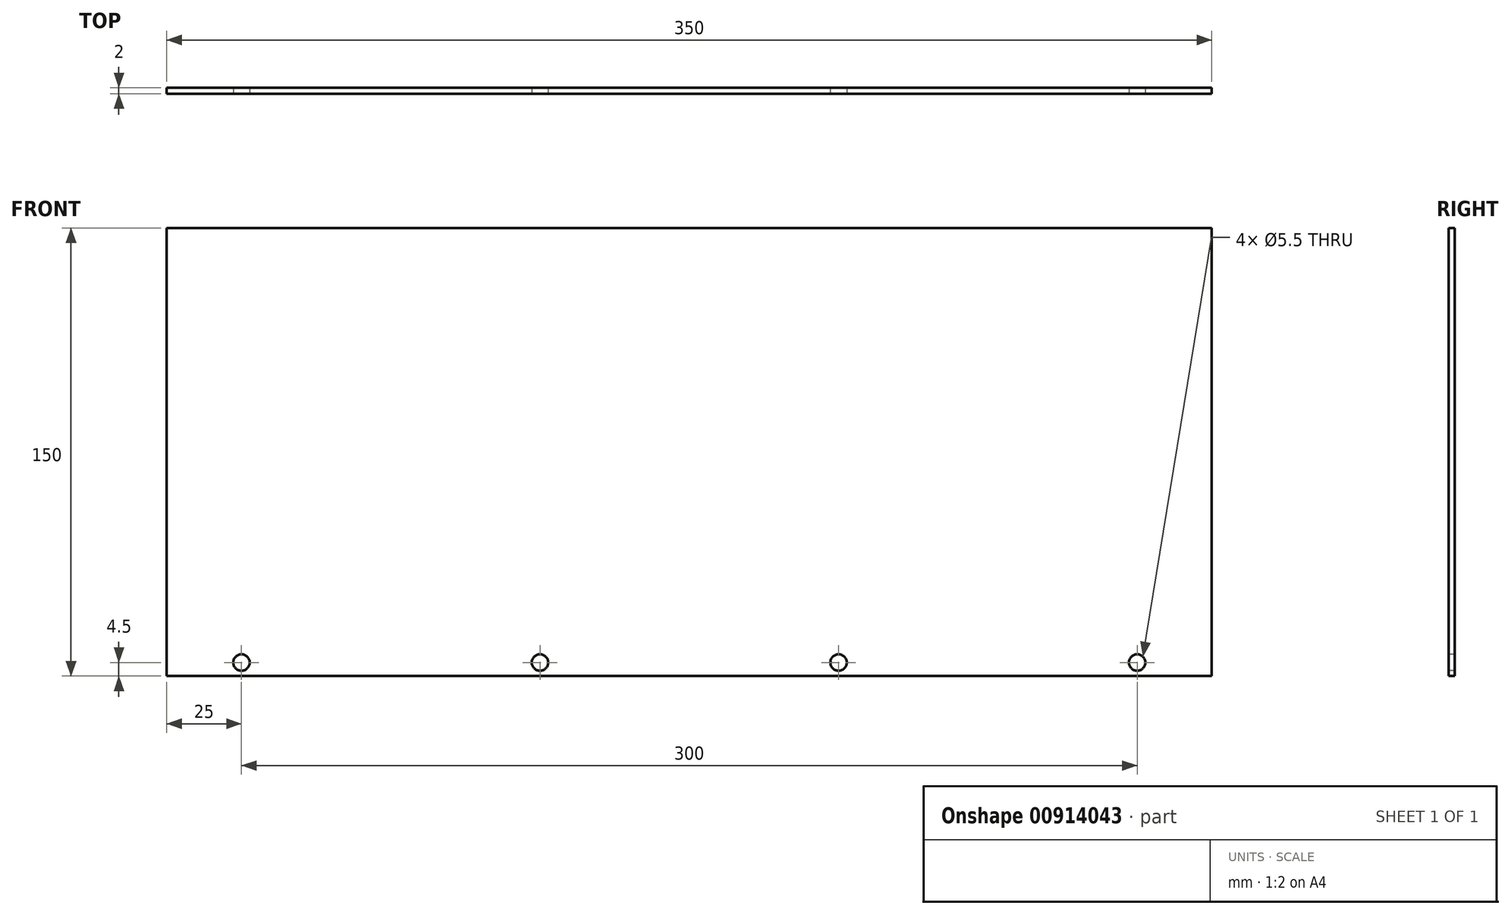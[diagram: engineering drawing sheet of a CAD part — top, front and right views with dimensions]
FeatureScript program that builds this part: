
annotation { "Feature Type Name" : "Feature", "Feature Type Description" : "" }
export const myFeature = defineFeature(function(context is Context, id is Id, definition is map)
    precondition{}
    {
        {
            var Q0;
            Q0=qCreatedBy(makeId("Front.planeOp"),FACE);
            var sketch = newSketch(context, id + "F0", { "sketchPlane" : qUnion([Q0])});
            skLineSegment(sketch, "E0.bottom", {"start": v(-175, 75) * mm, "end": v(175, 75) * mm});
            skLineSegment(sketch, "E0.top", {"start": v(-175, -75) * mm, "end": v(175, -75) * mm});
            skLineSegment(sketch, "E0.left", {"start": v(-175, 75) * mm, "end": v(-175, -75) * mm});
            skLineSegment(sketch, "E0.right", {"start": v(175, 75) * mm, "end": v(175, -75) * mm});
            skPoint(sketch, "E0.middle", {"position": v(0, 0) * mm});
            skSolve(sketch);
        }
        {
            var Q0;
            Q0=makeQuery(id+"F0.imprint","IMPRINT",FACE,{"disambiguationData":[TD([[makeQuery(id+"F0.imprint","IMPRINT",EDGE,{"derivedFrom":sQuery(id+"F0.wireOp",EDGE,"E0.bottom")}),-1.0]])]});
            extrude(context, id + "F1", {"entities" : qUnion([Q0]), "depth" : 2 * mm, "offsetDistance" : 25 * mm});
        }
        {
            var Q0;
            Q0=makeQuery(id+"F1.opExtrude","CAP_FACE",FACE,{"disambiguationData":[OSD([sQuery(id+"F0.wireOp",EDGE,"E0.bottom"),sQuery(id+"F0.wireOp",EDGE,"E0.top"),sQuery(id+"F0.wireOp",EDGE,"E0.left"),sQuery(id+"F0.wireOp",EDGE,"E0.right")])],"isStart":false});
            var sketch = newSketch(context, id + "F2", { "sketchPlane" : qUnion([Q0])});
            skLineSegment(sketch, "E1", {"start": v(-175, -70.5) * mm, "end": v(-150, -70.5) * mm});
            skLineSegment(sketch, "E2", {"start": v(-150, -70.5) * mm, "end": v(-50, -70.5) * mm});
            skLineSegment(sketch, "E3", {"start": v(-50, -70.5) * mm, "end": v(50, -70.5) * mm});
            skLineSegment(sketch, "E4", {"start": v(50, -70.5) * mm, "end": v(150, -70.5) * mm});
            skSolve(sketch);
        }
        {
            var Q0;
            Q0=sQuery(id+"F2.wireOp",VERTEX,"E1.end");
            var Q1;
            Q1=sQuery(id+"F2.wireOp",VERTEX,"E2.end");
            var Q2;
            Q2=sQuery(id+"F2.wireOp",VERTEX,"E3.end");
            var Q3;
            Q3=sQuery(id+"F2.wireOp",VERTEX,"E4.end");
            var Q4;
            Q4=makeQuery(id+"F1.opExtrude","SWEPT_BODY",BODY,{"disambiguationData":[OSD([sQuery(id+"F0.wireOp",EDGE,"E0.bottom"),sQuery(id+"F0.wireOp",EDGE,"E0.top"),sQuery(id+"F0.wireOp",EDGE,"E0.left"),sQuery(id+"F0.wireOp",EDGE,"E0.right")])]});
            hole(context, id + "F3", {"style" : HoleStyle.SIMPLE, "endStyle" : HoleEndStyle.BLIND, "standardTappedOrClearance" : lookupTablePath({ "fit" : "Normal", "standard" : "ISO", "size" : "M5", "type" : "Clearance" }), "standardBlindInLast" : lookupTablePath({ "fit" : "Normal", "standard" : "ISO", "size" : "M5", "type" : "Clearance" }), "holeDiameter" : 5.5 * mm, "majorDiameter" : 5 * mm, "holeDepth" : 13 * mm, "isTappedThrough" : true, "tappedDepth" : 10 * mm, "tapClearance" : 3, "startFromSketch" : true, "locations" : qUnion([Q0, Q1, Q2, Q3]), "scope" : qUnion([Q4])});
        }
    });
